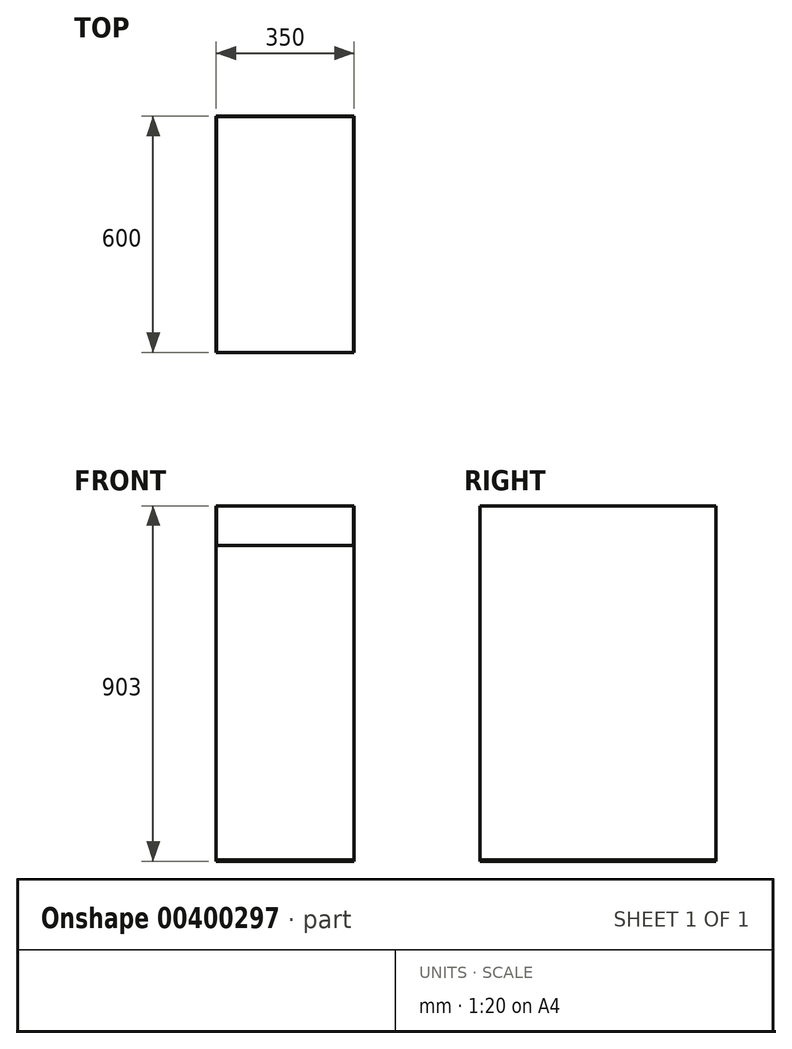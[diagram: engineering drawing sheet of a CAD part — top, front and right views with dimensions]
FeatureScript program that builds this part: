
annotation { "Feature Type Name" : "Feature", "Feature Type Description" : "" }
export const myFeature = defineFeature(function(context is Context, id is Id, definition is map)
    precondition{}
    {
        {
            var Q0;
            Q0=qCreatedBy(makeId("Top.planeOp"),FACE);
            var sketch = newSketch(context, id + "F0", { "sketchPlane" : qUnion([Q0])});
            skLineSegment(sketch, "E0.bottom", {"start": v(-175, 300) * mm, "end": v(175, 300) * mm});
            skLineSegment(sketch, "E0.top", {"start": v(-175, -300) * mm, "end": v(175, -300) * mm});
            skLineSegment(sketch, "E0.left", {"start": v(-175, 300) * mm, "end": v(-175, -300) * mm});
            skLineSegment(sketch, "E0.right", {"start": v(175, 300) * mm, "end": v(175, -300) * mm});
            skPoint(sketch, "E0.middle", {"position": v(0, 0) * mm});
            skSolve(sketch);
        }
        {
            var Q0;
            Q0=makeQuery(id+"F0.imprint","IMPRINT",FACE,{"disambiguationData":[TD([[makeQuery(id+"F0.imprint","IMPRINT",EDGE,{"derivedFrom":sQuery(id+"F0.wireOp",EDGE,"E0.bottom")}),-1.0]])]});
            extrude(context, id + "F1", {"entities" : qUnion([Q0]), "depth" : 3 * mm});
        }
        {
            var Q0;
            Q0=makeQuery(id+"F1.opExtrude","CAP_FACE",FACE,{"disambiguationData":[OSD([sQuery(id+"F0.wireOp",EDGE,"E0.bottom"),sQuery(id+"F0.wireOp",EDGE,"E0.top"),sQuery(id+"F0.wireOp",EDGE,"E0.left"),sQuery(id+"F0.wireOp",EDGE,"E0.right")])],"isStart":false});
            var sketch = newSketch(context, id + "F2", { "sketchPlane" : qUnion([Q0])});
            skLineSegment(sketch, "E1.0", {"start": v(-174, 299) * mm, "end": v(-174, -299) * mm});
            skLineSegment(sketch, "E1.1", {"start": v(174, 299) * mm, "end": v(-174, 299) * mm});
            skLineSegment(sketch, "E1.2", {"start": v(174, -299) * mm, "end": v(174, 299) * mm});
            skLineSegment(sketch, "E1.3", {"start": v(-174, -299) * mm, "end": v(174, -299) * mm});
            skLineSegment(sketch, "E2", {"start": v(-175, 300) * mm, "end": v(-174, 299) * mm});
            skLineSegment(sketch, "E3", {"start": v(175, 300) * mm, "end": v(174, 299) * mm});
            skLineSegment(sketch, "E4", {"start": v(174, -299) * mm, "end": v(175, -300) * mm});
            skLineSegment(sketch, "E5", {"start": v(175, -300) * mm, "end": v(-174, -299) * mm});
            skLineSegment(sketch, "E6", {"start": v(-174, -299) * mm, "end": v(-175, -300) * mm});
            skSolve(sketch);
        }
        {
            var Q0;
            Q0=makeQuery(id+"F2.imprint","IMPRINT",FACE,{"disambiguationData":[TD([[makeQuery(id+"F2.imprint","IMPRINT",EDGE,{"derivedFrom":sQuery(id+"F2.wireOp",EDGE,"E5")}),1.0]])]});
            extrude(context, id + "F3", {"entities" : qUnion([Q0]), "depth" : 800 * mm});
        }
        {
            var Q0;
            Q0=makeQuery(id+"F2.imprint","IMPRINT",FACE,{"disambiguationData":[TD([[makeQuery(id+"F2.imprint","IMPRINT",EDGE,{"derivedFrom":sQuery(id+"F2.wireOp",EDGE,"E1.0")}),-1.0]])]});
            extrude(context, id + "F4", {"entities" : qUnion([Q0]), "depth" : 900 * mm});
        }
        {
            var Q0;
            Q0=makeQuery(id+"F2.imprint","IMPRINT",FACE,{"disambiguationData":[TD([[makeQuery(id+"F2.imprint","IMPRINT",EDGE,{"derivedFrom":sQuery(id+"F2.wireOp",EDGE,"E1.2")}),-1.0]])]});
            extrude(context, id + "F5", {"entities" : qUnion([Q0]), "depth" : 900 * mm});
        }
        {
            var Q0;
            Q0=makeQuery(id+"F2.imprint","IMPRINT",FACE,{"disambiguationData":[TD([[makeQuery(id+"F2.imprint","IMPRINT",EDGE,{"derivedFrom":sQuery(id+"F2.wireOp",EDGE,"E1.1")}),-1.0]])]});
            extrude(context, id + "F6", {"entities" : qUnion([Q0]), "depth" : 900 * mm});
        }
    });
